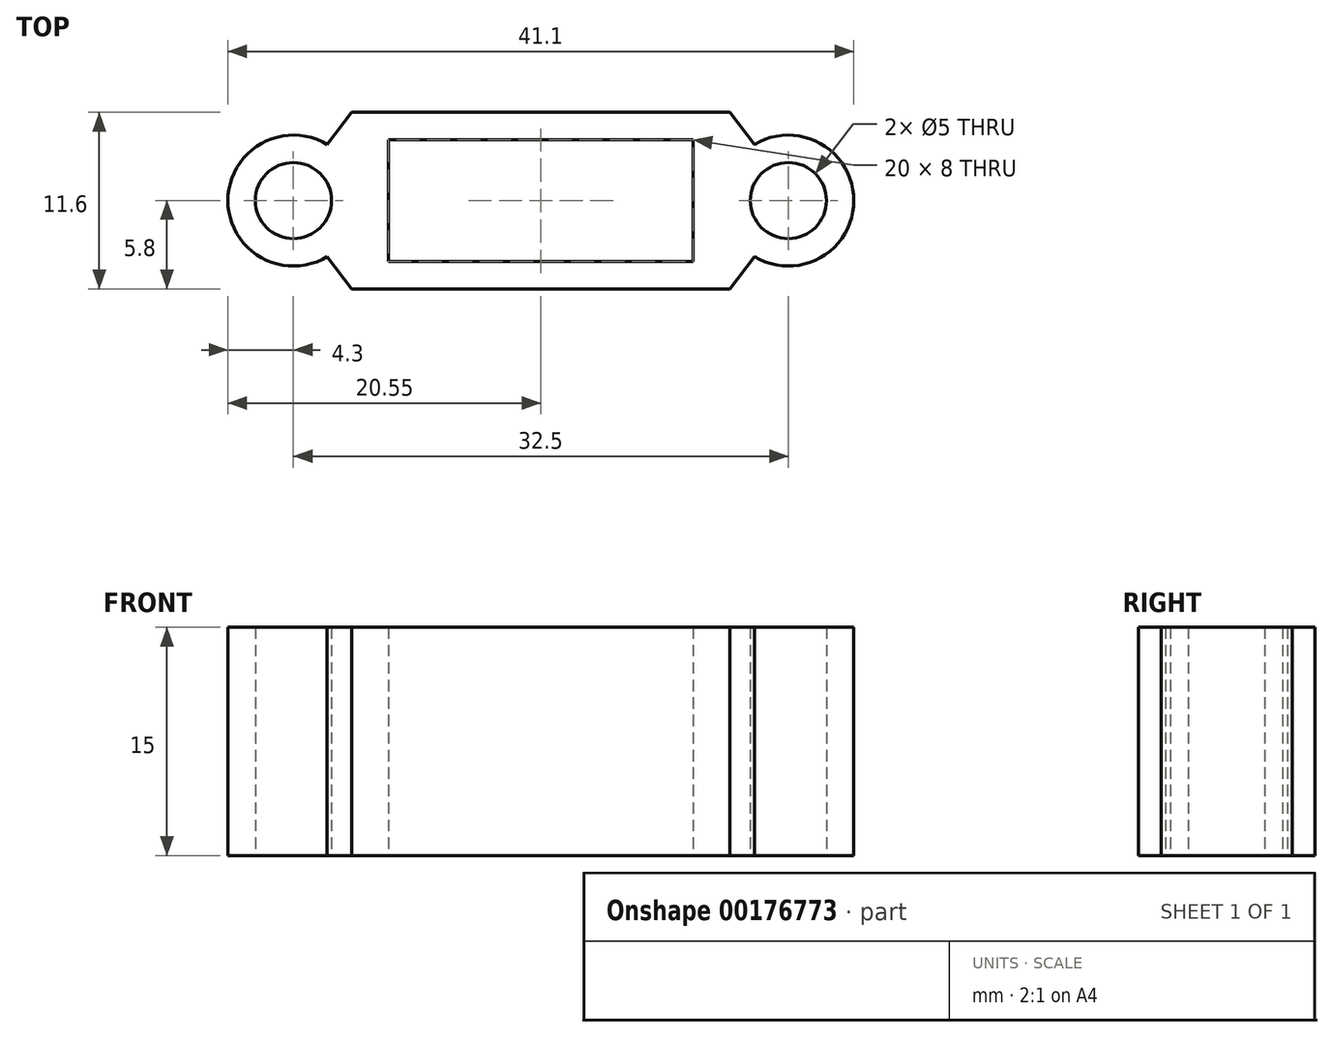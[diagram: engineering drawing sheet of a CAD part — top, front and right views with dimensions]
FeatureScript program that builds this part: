
annotation { "Feature Type Name" : "Feature", "Feature Type Description" : "" }
export const myFeature = defineFeature(function(context is Context, id is Id, definition is map)
    precondition{}
    {
        {
            assignVariable(context, id + "F0", {"name" : "pieceHeight", "anyValue" : 15});
        }
        {
            var Q0;
            Q0=qCreatedBy(makeId("Top.planeOp"),FACE);
            var sketch = newSketch(context, id + "F1", { "sketchPlane" : qUnion([Q0])});
            skCircle(sketch, "E0", {"center": v(-16.25, 0) * mm, "radius": 2.5 * mm});
            skCircle(sketch, "E1", {"center": v(16.25, 0) * mm, "radius": 2.5 * mm});
            skCircle(sketch, "E2.0", {"center": v(-16.25, 0) * mm, "radius": 4.3 * mm});
            skCircle(sketch, "E3.0", {"center": v(16.25, 0) * mm, "radius": 4.3 * mm});
            skLineSegment(sketch, "E4", {"start": v(-16.25, 0) * mm, "end": v(16.25, 0) * mm, "construction": true});
            skLineSegment(sketch, "E5.bottom", {"start": v(-10, 4) * mm, "end": v(10, 4) * mm});
            skLineSegment(sketch, "E5.top", {"start": v(-10, -4) * mm, "end": v(10, -4) * mm});
            skLineSegment(sketch, "E5.left", {"start": v(-10, 4) * mm, "end": v(-10, -4) * mm});
            skLineSegment(sketch, "E5.right", {"start": v(10, 4) * mm, "end": v(10, -4) * mm});
            skPoint(sketch, "E5.middle", {"position": v(0, 0) * mm});
            skLineSegment(sketch, "E6", {"start": v(-14.02, 3.68) * mm, "end": v(-12.4, 5.8) * mm});
            skLineSegment(sketch, "E7", {"start": v(-12.4, 5.8) * mm, "end": v(0, 5.8) * mm});
            skLineSegment(sketch, "E8", {"start": v(0, 5.8) * mm, "end": v(12.4, 5.8) * mm});
            skLineSegment(sketch, "E9", {"start": v(12.4, 5.8) * mm, "end": v(14.02, 3.68) * mm});
            skLineSegment(sketch, "E10.MirrorCS", {"start": v(0, -5.8) * mm, "end": v(12.4, -5.8) * mm});
            skLineSegment(sketch, "E11.MirrorCS", {"start": v(12.4, -5.8) * mm, "end": v(14.02, -3.68) * mm});
            skLineSegment(sketch, "E12.MirrorCS", {"start": v(-12.4, -5.8) * mm, "end": v(0, -5.8) * mm});
            skLineSegment(sketch, "E13.MirrorCS", {"start": v(-14.02, -3.68) * mm, "end": v(-12.4, -5.8) * mm});
            skSolve(sketch);
        }
        {
            var Q0;
            Q0=qSketchRegion(id+"F1",true);
            extrude(context, id + "F2", {"entities" : qUnion([Q0]), "depth" : (getVariable(context, 'pieceHeight')) * mm});
        }
    });
